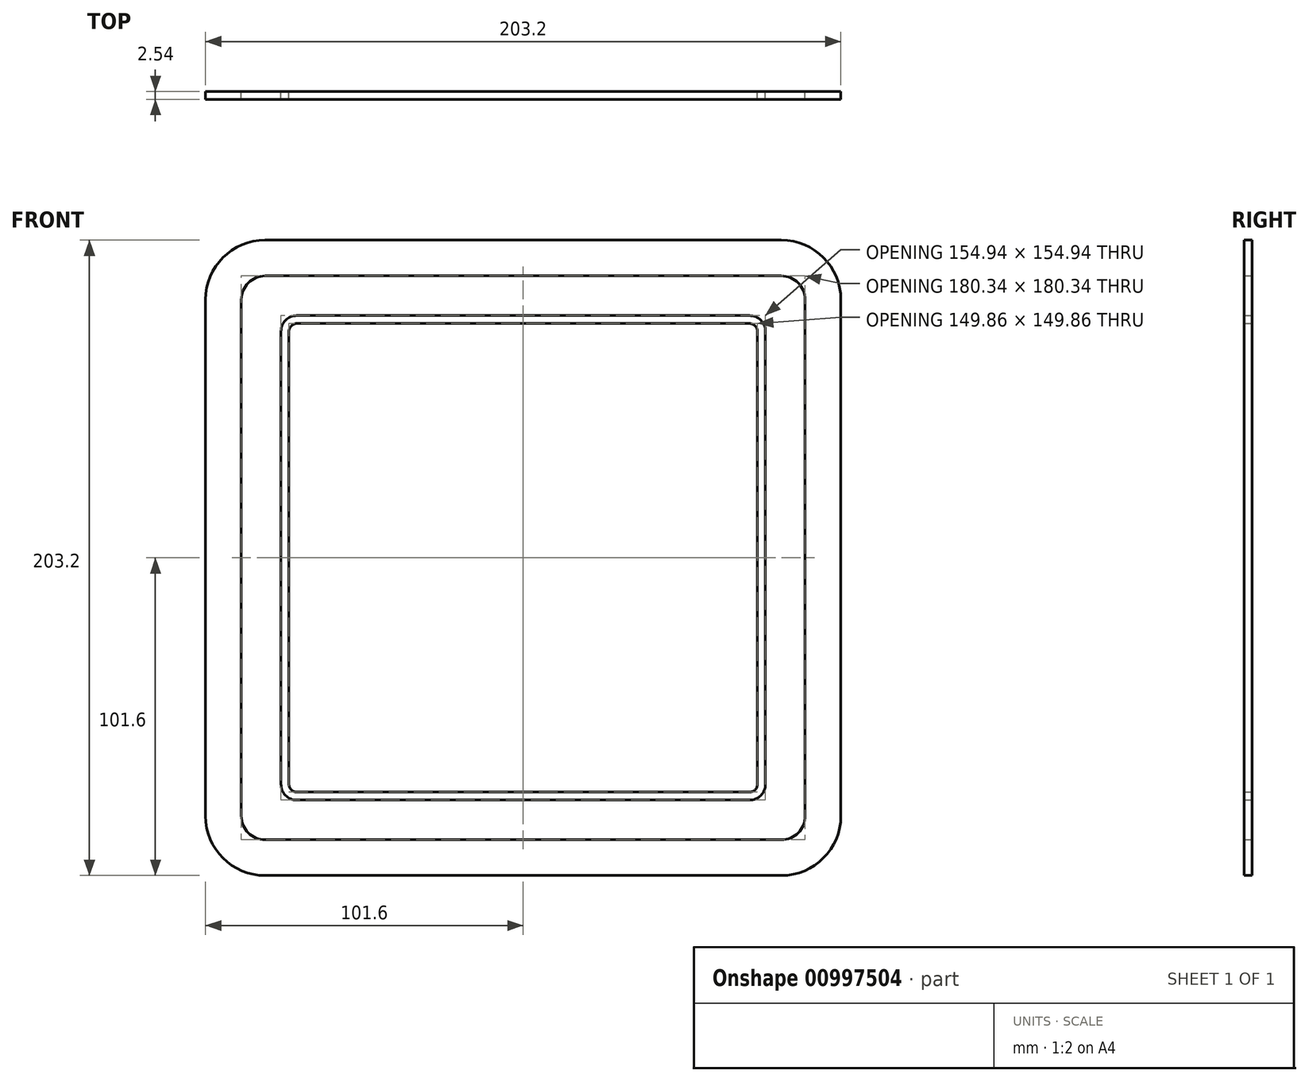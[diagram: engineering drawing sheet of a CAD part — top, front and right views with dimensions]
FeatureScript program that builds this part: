
annotation { "Feature Type Name" : "Feature", "Feature Type Description" : "" }
export const myFeature = defineFeature(function(context is Context, id is Id, definition is map)
    precondition{}
    {
        {
            var Q0;
            Q0=qCreatedBy(makeId("Front.planeOp"),FACE);
            var sketch = newSketch(context, id + "F0", { "sketchPlane" : qUnion([Q0])});
            skLineSegment(sketch, "E0", {"start": v(-101.6, 101.6) * mm, "end": v(-101.6, 54.02) * mm});
            skLineSegment(sketch, "E1", {"start": v(-101.6, 54.02) * mm, "end": v(-101.6, -15.92) * mm});
            skLineSegment(sketch, "E2", {"start": v(-101.6, -15.92) * mm, "end": v(-101.6, -63.5) * mm});
            skArc(sketch, "E3", {"start": v(-101.6, -63.5) * mm, "mid": v(-96.02, -76.97) * mm, "end": v(-82.55, -82.55) * mm});
            skLineSegment(sketch, "E4", {"start": v(-41.28, -82.55) * mm, "end": v(-82.55, -82.55) * mm});
            skLineSegment(sketch, "E5", {"start": v(82.55, -82.55) * mm, "end": v(41.28, -82.55) * mm});
            skArc(sketch, "E6", {"start": v(82.55, -82.55) * mm, "mid": v(96.02, -76.97) * mm, "end": v(101.6, -63.5) * mm});
            skLineSegment(sketch, "E7", {"start": v(101.6, 101.6) * mm, "end": v(101.6, -63.5) * mm});
            skArc(sketch, "E8", {"start": v(101.6, 101.6) * mm, "mid": v(96.02, 115.07) * mm, "end": v(82.55, 120.65) * mm});
            skLineSegment(sketch, "E9", {"start": v(82.55, 120.65) * mm, "end": v(-82.55, 120.65) * mm});
            skArc(sketch, "E10", {"start": v(-82.55, 120.65) * mm, "mid": v(-96.02, 115.07) * mm, "end": v(-101.6, 101.6) * mm});
            skLineSegment(sketch, "E11", {"start": v(72.4, 93.98) * mm, "end": v(-72.4, 93.98) * mm});
            skArc(sketch, "E12", {"start": v(74.93, 91.44) * mm, "mid": v(74.19, 93.24) * mm, "end": v(72.4, 93.98) * mm});
            skLineSegment(sketch, "E13", {"start": v(74.93, 91.44) * mm, "end": v(74.93, -53.34) * mm});
            skArc(sketch, "E14", {"start": v(72.4, -55.88) * mm, "mid": v(74.19, -55.14) * mm, "end": v(74.93, -53.34) * mm});
            skLineSegment(sketch, "E15", {"start": v(72.4, -55.88) * mm, "end": v(-72.4, -55.88) * mm});
            skArc(sketch, "E16", {"start": v(-74.93, -53.34) * mm, "mid": v(-74.19, -55.14) * mm, "end": v(-72.39, -55.88) * mm});
            skLineSegment(sketch, "E17", {"start": v(-74.93, 91.44) * mm, "end": v(-74.93, -53.34) * mm});
            skArc(sketch, "E18", {"start": v(-72.39, 93.98) * mm, "mid": v(-74.19, 93.24) * mm, "end": v(-74.93, 91.44) * mm});
            skLineSegment(sketch, "E19", {"start": v(-41.28, -82.55) * mm, "end": v(41.28, -82.55) * mm});
            skArc(sketch, "E20.0", {"start": v(-82.55, 109.22) * mm, "mid": v(-87.94, 106.99) * mm, "end": v(-90.17, 101.6) * mm});
            skLineSegment(sketch, "E20.1", {"start": v(-41.28, -71.12) * mm, "end": v(-82.55, -71.12) * mm});
            skArc(sketch, "E20.2", {"start": v(-90.17, -63.5) * mm, "mid": v(-87.94, -68.89) * mm, "end": v(-82.55, -71.12) * mm});
            skLineSegment(sketch, "E20.3", {"start": v(-90.17, -15.92) * mm, "end": v(-90.17, -63.5) * mm});
            skLineSegment(sketch, "E20.4", {"start": v(-90.17, 54.02) * mm, "end": v(-90.17, -15.92) * mm});
            skLineSegment(sketch, "E20.5", {"start": v(-41.28, -71.12) * mm, "end": v(41.28, -71.12) * mm});
            skLineSegment(sketch, "E20.6", {"start": v(-90.17, 101.6) * mm, "end": v(-90.17, 54.02) * mm});
            skLineSegment(sketch, "E20.7", {"start": v(82.55, -71.12) * mm, "end": v(41.28, -71.12) * mm});
            skArc(sketch, "E20.8", {"start": v(82.55, -71.12) * mm, "mid": v(87.94, -68.89) * mm, "end": v(90.17, -63.5) * mm});
            skLineSegment(sketch, "E20.9", {"start": v(90.17, 101.6) * mm, "end": v(90.17, -63.5) * mm});
            skArc(sketch, "E20.10", {"start": v(90.17, 101.6) * mm, "mid": v(87.94, 106.99) * mm, "end": v(82.55, 109.22) * mm});
            skLineSegment(sketch, "E20.11", {"start": v(82.55, 109.22) * mm, "end": v(-82.55, 109.22) * mm});
            skArc(sketch, "E21.0", {"start": v(77.47, 91.44) * mm, "mid": v(75.98, 95.03) * mm, "end": v(72.4, 96.52) * mm});
            skLineSegment(sketch, "E21.1", {"start": v(77.47, 91.44) * mm, "end": v(77.47, -53.34) * mm});
            skLineSegment(sketch, "E21.2", {"start": v(72.4, 96.52) * mm, "end": v(-72.4, 96.52) * mm});
            skArc(sketch, "E21.3", {"start": v(72.4, -58.42) * mm, "mid": v(75.98, -56.93) * mm, "end": v(77.47, -53.34) * mm});
            skArc(sketch, "E21.4", {"start": v(-72.4, 96.52) * mm, "mid": v(-75.98, 95.03) * mm, "end": v(-77.47, 91.44) * mm});
            skLineSegment(sketch, "E21.5", {"start": v(-77.47, 91.44) * mm, "end": v(-77.47, -53.34) * mm});
            skArc(sketch, "E21.6", {"start": v(-77.47, -53.34) * mm, "mid": v(-75.98, -56.93) * mm, "end": v(-72.39, -58.42) * mm});
            skLineSegment(sketch, "E21.7", {"start": v(72.4, -58.42) * mm, "end": v(-72.4, -58.42) * mm});
            skSolve(sketch);
        }
        {
            var Q0;
            Q0=makeQuery(id+"F0.imprint","IMPRINT",FACE,{"disambiguationData":[TD([[makeQuery(id+"F0.imprint","IMPRINT",EDGE,{"derivedFrom":sQuery(id+"F0.wireOp",EDGE,"E0")}),1.0]])]});
            var Q1;
            Q1=makeQuery(id+"F0.imprint","IMPRINT",FACE,{"disambiguationData":[TD([[makeQuery(id+"F0.imprint","IMPRINT",EDGE,{"derivedFrom":sQuery(id+"F0.wireOp",EDGE,"E11")}),-1.0]])]});
            extrude(context, id + "F1", {"entities" : qUnion([Q0, Q1]), "depth" : 2.54 * mm, "offsetDistance" : 25.4 * mm});
        }
        {
            var Q0;
            Q0=makeQuery(id+"F0.imprint","IMPRINT",FACE,{"disambiguationData":[TD([[makeQuery(id+"F0.imprint","IMPRINT",EDGE,{"derivedFrom":sQuery(id+"F0.wireOp",EDGE,"E20.0")}),1.0]])]});
            extrude(context, id + "F2", {"entities" : qUnion([Q0]), "depth" : 2.54 * mm, "offsetDistance" : 25.4 * mm});
        }
    });
